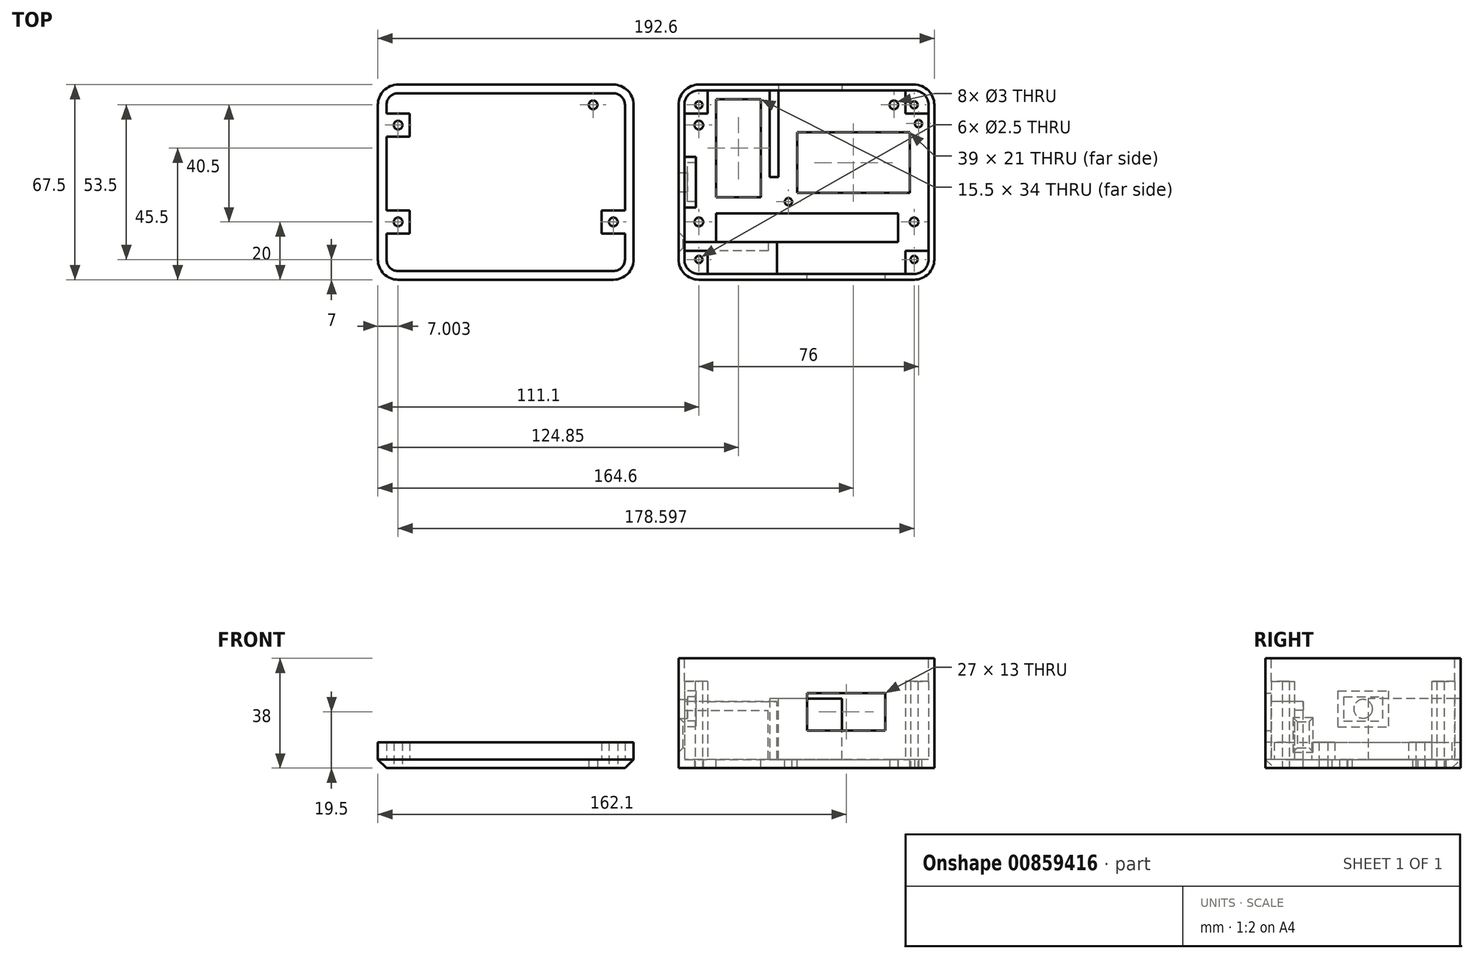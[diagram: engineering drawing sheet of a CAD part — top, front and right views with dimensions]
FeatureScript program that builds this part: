
annotation { "Feature Type Name" : "Feature", "Feature Type Description" : "" }
export const myFeature = defineFeature(function(context is Context, id is Id, definition is map)
    precondition{}
    {
        {
            var Q0;
            Q0=qCreatedBy(makeId("Top.planeOp"),FACE);
            var sketch = newSketch(context, id + "F0", { "sketchPlane" : qUnion([Q0])});
            skLineSegment(sketch, "E0.bottom", {"start": v(37.25, -30.75) * mm, "end": v(-37.25, -30.75) * mm});
            skLineSegment(sketch, "E0.top", {"start": v(37.25, 30.75) * mm, "end": v(-37.25, 30.75) * mm});
            skLineSegment(sketch, "E0.left", {"start": v(41.25, -26.75) * mm, "end": v(41.25, 26.75) * mm});
            skLineSegment(sketch, "E0.right", {"start": v(-41.25, -26.75) * mm, "end": v(-41.25, 26.75) * mm});
            skPoint(sketch, "E0.middle", {"position": v(0, 0) * mm});
            skPoint(sketch, "E1", {"position": v(-41.25, -26.75) * mm});
            skPoint(sketch, "E2", {"position": v(-41.25, 26.75) * mm});
            skPoint(sketch, "E3", {"position": v(37.25, -30.75) * mm});
            skPoint(sketch, "E4", {"position": v(-37.25, -30.75) * mm});
            skLineSegment(sketch, "E5", {"start": v(-41.25, 26.75) * mm, "end": v(41.25, 26.75) * mm, "construction": true});
            skLineSegment(sketch, "E6", {"start": v(-41.25, -26.75) * mm, "end": v(41.25, -26.75) * mm, "construction": true});
            skLineSegment(sketch, "E7", {"start": v(-37.25, -30.75) * mm, "end": v(-37.25, 30.75) * mm, "construction": true});
            skLineSegment(sketch, "E8", {"start": v(37.25, -30.75) * mm, "end": v(37.25, 30.75) * mm, "construction": true});
            skPoint(sketch, "E9", {"position": v(-37.25, 26.75) * mm});
            skPoint(sketch, "E10", {"position": v(37.25, 26.75) * mm});
            skPoint(sketch, "E11", {"position": v(37.25, -26.75) * mm});
            skPoint(sketch, "E12", {"position": v(-37.25, -26.75) * mm});
            skCircle(sketch, "E13", {"center": v(-37.25, 26.75) * mm, "radius": 1.25 * mm});
            skCircle(sketch, "E14", {"center": v(37.25, 26.75) * mm, "radius": 1.25 * mm});
            skCircle(sketch, "E15", {"center": v(-37.25, -26.75) * mm, "radius": 1.25 * mm});
            skCircle(sketch, "E16", {"center": v(37.25, -26.75) * mm, "radius": 1.25 * mm});
            skPoint(sketch, "E17.visualSharp", {"position": v(-41.25, 30.75) * mm});
            skArc(sketch, "E17.filletArc", {"start": v(-37.25, 30.75) * mm, "mid": v(-40.08, 29.58) * mm, "end": v(-41.25, 26.75) * mm});
            skPoint(sketch, "E18.visualSharp", {"position": v(41.25, 30.75) * mm});
            skArc(sketch, "E18.filletArc", {"start": v(41.25, 26.75) * mm, "mid": v(40.08, 29.58) * mm, "end": v(37.25, 30.75) * mm});
            skPoint(sketch, "E19.visualSharp", {"position": v(41.25, -30.75) * mm});
            skArc(sketch, "E19.filletArc", {"start": v(37.25, -30.75) * mm, "mid": v(40.08, -29.58) * mm, "end": v(41.25, -26.75) * mm});
            skPoint(sketch, "E20.visualSharp", {"position": v(-41.25, -30.75) * mm});
            skArc(sketch, "E20.filletArc", {"start": v(-41.25, -26.75) * mm, "mid": v(-40.08, -29.58) * mm, "end": v(-37.25, -30.75) * mm});
            skArc(sketch, "E21.0", {"start": v(44.25, 26.75) * mm, "mid": v(42.2, 31.7) * mm, "end": v(37.25, 33.75) * mm});
            skLineSegment(sketch, "E21.1", {"start": v(44.25, -26.75) * mm, "end": v(44.25, 26.75) * mm});
            skLineSegment(sketch, "E21.2", {"start": v(37.25, 33.75) * mm, "end": v(-37.25, 33.75) * mm});
            skArc(sketch, "E21.3", {"start": v(37.25, -33.75) * mm, "mid": v(42.2, -31.7) * mm, "end": v(44.25, -26.75) * mm});
            skArc(sketch, "E21.4", {"start": v(-37.25, 33.75) * mm, "mid": v(-42.2, 31.7) * mm, "end": v(-44.25, 26.75) * mm});
            skLineSegment(sketch, "E21.5", {"start": v(-44.25, -26.75) * mm, "end": v(-44.25, 26.75) * mm});
            skArc(sketch, "E21.6", {"start": v(-44.25, -26.75) * mm, "mid": v(-42.2, -31.7) * mm, "end": v(-37.25, -33.75) * mm});
            skLineSegment(sketch, "E21.7", {"start": v(37.25, -33.75) * mm, "end": v(-37.25, -33.75) * mm});
            skPoint(sketch, "E22", {"position": v(-41.25, 23.75) * mm});
            skPoint(sketch, "E23", {"position": v(-34.25, 30.75) * mm});
            skPoint(sketch, "E24", {"position": v(-41.25, -23.75) * mm});
            skPoint(sketch, "E25", {"position": v(-34.25, -30.75) * mm});
            skPoint(sketch, "E26", {"position": v(34.25, -30.75) * mm});
            skPoint(sketch, "E27", {"position": v(41.25, -23.75) * mm});
            skPoint(sketch, "E28", {"position": v(34.25, 30.75) * mm});
            skPoint(sketch, "E29", {"position": v(41.25, 23.75) * mm});
            skLineSegment(sketch, "E30", {"start": v(34.25, 30.75) * mm, "end": v(34.25, 23.75) * mm});
            skLineSegment(sketch, "E31", {"start": v(34.25, 23.75) * mm, "end": v(41.25, 23.75) * mm});
            skLineSegment(sketch, "E32", {"start": v(41.25, -23.75) * mm, "end": v(34.25, -23.75) * mm});
            skLineSegment(sketch, "E33", {"start": v(34.25, -23.75) * mm, "end": v(34.25, -30.75) * mm});
            skLineSegment(sketch, "E34", {"start": v(-34.25, -30.75) * mm, "end": v(-34.25, -23.75) * mm});
            skLineSegment(sketch, "E35", {"start": v(-34.25, -23.75) * mm, "end": v(-41.25, -23.75) * mm});
            skLineSegment(sketch, "E36", {"start": v(-41.25, 23.75) * mm, "end": v(-34.25, 23.75) * mm});
            skLineSegment(sketch, "E37", {"start": v(-34.25, 23.75) * mm, "end": v(-34.25, 30.75) * mm});
            skPoint(sketch, "E38", {"position": v(-37.25, -13.75) * mm});
            skPoint(sketch, "E39", {"position": v(37.25, -13.75) * mm});
            skPoint(sketch, "E40", {"position": v(-37.25, 19.75) * mm});
            skPoint(sketch, "E41", {"position": v(30.25, 26.75) * mm});
            skCircle(sketch, "E42", {"center": v(-37.25, 19.75) * mm, "radius": 1.5 * mm});
            skCircle(sketch, "E43", {"center": v(-37.25, -13.75) * mm, "radius": 1.5 * mm});
            skCircle(sketch, "E44", {"center": v(30.25, 26.75) * mm, "radius": 1.5 * mm});
            skCircle(sketch, "E45", {"center": v(37.25, -13.75) * mm, "radius": 1.5 * mm});
            skSolve(sketch);
        }
        {
            var Q0;
            {var subQ7=sQuery(id+"F0.wireOp",EDGE,"E30");Q0=makeQuery(id+"F0.imprint","IMPRINT",FACE,{"disambiguationData":[TD([[makeQuery(id+"F0.imprint","IMPRINT",EDGE,{"derivedFrom":subQ7}),-1.0]])]});}
            extrude(context, id + "F1", {"entities" : qUnion([Q0]), "depth" : 3 * mm, "offsetDistance" : 25 * mm});
        }
        {
            var Q0;
            Q0=makeQuery(id+"F0.imprint","IMPRINT",FACE,{"disambiguationData":[TD([[makeQuery(id+"F0.imprint","IMPRINT",EDGE,{"derivedFrom":sQuery(id+"F0.wireOp",EDGE,"E0.bottom")}),1.0]])]});
            extrude(context, id + "F2", {"entities" : qUnion([Q0]), "operationType" : NewBodyOperationType.ADD, "depth" : 38 * mm, "offsetDistance" : 25 * mm});
        }
        {
            var Q0;
            Q0=makeQuery(id+"F0.imprint","IMPRINT",FACE,{"disambiguationData":[TD([[makeQuery(id+"F0.imprint","IMPRINT",EDGE,{"derivedFrom":sQuery(id+"F0.wireOp",EDGE,"E13")}),-1.0]])]});
            var Q1;
            Q1=makeQuery(id+"F0.imprint","IMPRINT",FACE,{"disambiguationData":[TD([[makeQuery(id+"F0.imprint","IMPRINT",EDGE,{"derivedFrom":sQuery(id+"F0.wireOp",EDGE,"E15")}),-1.0]])]});
            var Q2;
            Q2=makeQuery(id+"F0.imprint","IMPRINT",FACE,{"disambiguationData":[TD([[makeQuery(id+"F0.imprint","IMPRINT",EDGE,{"derivedFrom":sQuery(id+"F0.wireOp",EDGE,"E14")}),-1.0]])]});
            var Q3;
            Q3=makeQuery(id+"F0.imprint","IMPRINT",FACE,{"disambiguationData":[TD([[makeQuery(id+"F0.imprint","IMPRINT",EDGE,{"derivedFrom":sQuery(id+"F0.wireOp",EDGE,"E16")}),-1.0]])]});
            extrude(context, id + "F3", {"entities" : qUnion([Q0, Q1, Q2, Q3]), "operationType" : NewBodyOperationType.ADD, "depth" : 30 * mm, "offsetDistance" : 25 * mm});
        }
        {
            var Q0;
            Q0=makeQuery(id+"F2.opExtrude","SWEPT_FACE",FACE,{"disambiguationData":[OSD([sQuery(id+"F0.wireOp",EDGE,"E0.bottom")])]});
            var sketch = newSketch(context, id + "F4", { "sketchPlane" : qUnion([Q0])});
            skLineSegment(sketch, "E46.bottom", {"start": v(34.25, 3) * mm, "end": v(13.25, 3) * mm});
            skLineSegment(sketch, "E46.top", {"start": v(34.25, 20) * mm, "end": v(13.25, 20) * mm});
            skLineSegment(sketch, "E46.left", {"start": v(34.25, 3) * mm, "end": v(34.25, 20) * mm});
            skLineSegment(sketch, "E46.right", {"start": v(13.25, 3) * mm, "end": v(13.25, 20) * mm});
            skLineSegment(sketch, "E47.0", {"start": v(10.25, 3) * mm, "end": v(10.25, 23) * mm});
            skLineSegment(sketch, "E47.1", {"start": v(34.25, 23) * mm, "end": v(10.25, 23) * mm});
            skLineSegment(sketch, "E48", {"start": v(34.25, 23) * mm, "end": v(34.25, 20) * mm});
            skLineSegment(sketch, "E49", {"start": v(13.25, 3) * mm, "end": v(10.25, 3) * mm});
            skPoint(sketch, "E50", {"position": v(-13.25, 3) * mm});
            skPoint(sketch, "E51", {"position": v(-13.25, 16) * mm});
            skLineSegment(sketch, "E52.top", {"start": v(-3.25, 26) * mm, "end": v(-27.25, 26) * mm});
            skLineSegment(sketch, "E52.right", {"start": v(-27.25, 16) * mm, "end": v(-27.25, 26) * mm});
            skLineSegment(sketch, "E53.0", {"start": v(-0.25, 13) * mm, "end": v(-0.25, 26) * mm});
            skLineSegment(sketch, "E53.1", {"start": v(-0.25, 13) * mm, "end": v(-27.25, 13) * mm});
            skLineSegment(sketch, "E54", {"start": v(-0.25, 26) * mm, "end": v(-3.25, 26) * mm});
            skLineSegment(sketch, "E55", {"start": v(-27.25, 13) * mm, "end": v(-27.25, 16) * mm});
            skSolve(sketch);
        }
        {
            var Q0;
            Q0=makeQuery(id+"F4.imprint","IMPRINT",FACE,{"disambiguationData":[TD([[makeQuery(id+"F4.imprint","IMPRINT",EDGE,{"derivedFrom":sQuery(id+"F4.wireOp",EDGE,"E46.top")}),-1.0]])]});
            var Q1;
            Q1=makeQuery(id+"F4.imprint","IMPRINT",FACE,{"disambiguationData":[TD([[makeQuery(id+"F4.imprint","IMPRINT",EDGE,{"derivedFrom":sQuery(id+"F4.wireOp",EDGE,"E46.bottom")}),1.0]])]});
            extrude(context, id + "F5", {"entities" : qUnion([Q0, Q1]), "operationType" : NewBodyOperationType.ADD, "depth" : 7 * mm, "offsetDistance" : 25 * mm});
        }
        {
            var Q0;
            Q0=makeQuery(id+"F5.boolean.opBoolean","MERGE",FACE,{"derivedFrom":[makeQuery(id+"F3.opExtrude","SWEPT_FACE",FACE,{"disambiguationData":[OSD([sQuery(id+"F0.wireOp",EDGE,"E35")])]}),makeQuery(id+"F5.opExtrude","CAP_FACE",FACE,{"disambiguationData":[OSD([sQuery(id+"F4.wireOp",EDGE,"E46.bottom"),sQuery(id+"F4.wireOp",EDGE,"E46.left"),sQuery(id+"F4.wireOp",EDGE,"E47.0"),sQuery(id+"F4.wireOp",EDGE,"E47.1"),sQuery(id+"F4.wireOp",EDGE,"E48"),sQuery(id+"F4.wireOp",EDGE,"E49")])],"isStart":false})]});
            var sketch = newSketch(context, id + "F6", { "sketchPlane" : qUnion([Q0])});
            skLineSegment(sketch, "E56", {"start": v(34.25, 23) * mm, "end": v(41.25, 23) * mm});
            skLineSegment(sketch, "E57.bottom", {"start": v(41.25, 3) * mm, "end": v(13.25, 3) * mm});
            skLineSegment(sketch, "E57.top", {"start": v(41.25, 20) * mm, "end": v(13.25, 20) * mm});
            skLineSegment(sketch, "E57.left", {"start": v(41.25, 3) * mm, "end": v(41.25, 20) * mm});
            skLineSegment(sketch, "E57.right", {"start": v(13.25, 3) * mm, "end": v(13.25, 20) * mm});
            skSolve(sketch);
        }
        {
            var Q0;
            {var subQ3=sQuery(id+"F6.wireOp",EDGE,"E56");Q0=makeQuery(id+"F6.imprint","IMPRINT",FACE,{"disambiguationData":[TD([[makeQuery(id+"F6.imprint","IMPRINT",EDGE,{"derivedFrom":subQ3}),-1.0]])]});}
            extrude(context, id + "F7", {"entities" : qUnion([Q0]), "operationType" : NewBodyOperationType.ADD, "depth" : 3 * mm, "offsetDistance" : 25 * mm});
        }
        {
            var Q0;
            Q0=makeQuery(id+"F2.opExtrude","SWEPT_FACE",FACE,{"disambiguationData":[OSD([sQuery(id+"F0.wireOp",EDGE,"E0.right")])]});
            var sketch = newSketch(context, id + "F8", { "sketchPlane" : qUnion([Q0])});
            skPoint(sketch, "E58", {"position": v(-23.75, 11.5) * mm});
            skPoint(sketch, "E59", {"position": v(-23.75, 16) * mm});
            skPoint(sketch, "E60", {"position": v(-23.75, 7) * mm});
            skLineSegment(sketch, "E61.bottom", {"start": v(-23.75, 16) * mm, "end": v(-18.75, 16) * mm});
            skLineSegment(sketch, "E61.top", {"start": v(-23.75, 7) * mm, "end": v(-18.75, 7) * mm});
            skLineSegment(sketch, "E61.right", {"start": v(-18.75, 16) * mm, "end": v(-18.75, 7) * mm});
            skPoint(sketch, "E62", {"position": v(-22.75, 16) * mm});
            skLineSegment(sketch, "E63", {"start": v(-22.75, 16) * mm, "end": v(-22.75, 7) * mm});
            skLineSegment(sketch, "E64", {"start": v(0, 3) * mm, "end": v(0, 38) * mm, "construction": true});
            skPoint(sketch, "E65", {"position": v(0, 20.5) * mm});
            skCircle(sketch, "E66", {"center": v(0, 20.5) * mm, "radius": 3.25 * mm});
            skLineSegment(sketch, "E67.bottom", {"start": v(-6.75, 24.75) * mm, "end": v(6.75, 24.75) * mm});
            skLineSegment(sketch, "E67.top", {"start": v(-6.75, 16.25) * mm, "end": v(6.75, 16.25) * mm});
            skLineSegment(sketch, "E67.left", {"start": v(-6.75, 24.75) * mm, "end": v(-6.75, 16.25) * mm});
            skLineSegment(sketch, "E67.right", {"start": v(6.75, 24.75) * mm, "end": v(6.75, 16.25) * mm});
            skLineSegment(sketch, "E68.0", {"start": v(-8.75, 26.75) * mm, "end": v(8.75, 26.75) * mm});
            skLineSegment(sketch, "E68.1", {"start": v(-8.75, 26.75) * mm, "end": v(-8.75, 14.25) * mm});
            skLineSegment(sketch, "E68.2", {"start": v(-8.75, 14.25) * mm, "end": v(8.75, 14.25) * mm});
            skLineSegment(sketch, "E68.3", {"start": v(8.75, 26.75) * mm, "end": v(8.75, 14.25) * mm});
            skSolve(sketch);
        }
        {
            var Q0;
            {var subQ0=sQuery(id+"F8.wireOp",EDGE,"E61.right");Q0=makeQuery(id+"F8.imprint","IMPRINT",FACE,{"disambiguationData":[TD([[makeQuery(id+"F8.imprint","IMPRINT",EDGE,{"derivedFrom":subQ0}),-1.0]])]});}
            extrude(context, id + "F9", {"entities" : qUnion([Q0]), "operationType" : NewBodyOperationType.REMOVE, "oppositeDirection" : true, "depth" : 25 * mm, "offsetDistance" : 25 * mm});
        }
        {
            var Q0;
            Q0=makeQuery(id+"F9.boolean.opBoolean","INTERSECT",EDGE,{"derivedFrom":[makeQuery(id+"F2.opExtrude","SWEPT_FACE",FACE,{"disambiguationData":[OSD([sQuery(id+"F0.wireOp",EDGE,"E21.5")])]}),makeQuery(id+"F9.opExtrude","SWEPT_FACE",FACE,{"disambiguationData":[OSD([sQuery(id+"F8.wireOp",EDGE,"E61.right")])]})]});
            var Q1;
            Q1=makeQuery(id+"F9.boolean.opBoolean","INTERSECT",EDGE,{"derivedFrom":[makeQuery(id+"F2.opExtrude","SWEPT_FACE",FACE,{"disambiguationData":[OSD([sQuery(id+"F0.wireOp",EDGE,"E21.5")])]}),makeQuery(id+"F9.opExtrude","SWEPT_FACE",FACE,{"disambiguationData":[OSD([sQuery(id+"F8.wireOp",EDGE,"E61.top")])]})]});
            var Q2;
            Q2=makeQuery(id+"F9.boolean.opBoolean","INTERSECT",EDGE,{"derivedFrom":[makeQuery(id+"F2.opExtrude","SWEPT_FACE",FACE,{"disambiguationData":[OSD([sQuery(id+"F0.wireOp",EDGE,"E21.5")])]}),makeQuery(id+"F9.opExtrude","SWEPT_FACE",FACE,{"disambiguationData":[OSD([sQuery(id+"F8.wireOp",EDGE,"E63")])]})]});
            var Q3;
            Q3=makeQuery(id+"F9.boolean.opBoolean","INTERSECT",EDGE,{"derivedFrom":[makeQuery(id+"F2.opExtrude","SWEPT_FACE",FACE,{"disambiguationData":[OSD([sQuery(id+"F0.wireOp",EDGE,"E21.5")])]}),makeQuery(id+"F9.opExtrude","SWEPT_FACE",FACE,{"disambiguationData":[OSD([sQuery(id+"F8.wireOp",EDGE,"E61.bottom")])]})]});
            chamfer(context, id + "F10", {"entities" : qUnion([Q0, Q1, Q2, Q3]), "width" : 1.5 * mm, "tangentPropagation" : true});
        }
        {
            var Q0;
            Q0=makeQuery(id+"F1.opExtrude","CAP_FACE",FACE,{"disambiguationData":[OSD([sQuery(id+"F0.wireOp",EDGE,"E0.bottom"),sQuery(id+"F0.wireOp",EDGE,"E0.top"),sQuery(id+"F0.wireOp",EDGE,"E0.left"),sQuery(id+"F0.wireOp",EDGE,"E0.right"),sQuery(id+"F0.wireOp",EDGE,"E30"),sQuery(id+"F0.wireOp",EDGE,"E31"),sQuery(id+"F0.wireOp",EDGE,"E32"),sQuery(id+"F0.wireOp",EDGE,"E33"),sQuery(id+"F0.wireOp",EDGE,"E34"),sQuery(id+"F0.wireOp",EDGE,"E35"),sQuery(id+"F0.wireOp",EDGE,"E36"),sQuery(id+"F0.wireOp",EDGE,"E37")])],"isStart":false});
            var sketch = newSketch(context, id + "F11", { "sketchPlane" : qUnion([Q0])});
            skPoint(sketch, "E69", {"position": v(12.25, 21.25) * mm});
            skPoint(sketch, "E70", {"position": v(-8.75, 21.25) * mm});
            skPoint(sketch, "E71", {"position": v(-8.75, 30.75) * mm});
            skPoint(sketch, "E72", {"position": v(12.25, 30.75) * mm});
            skLineSegment(sketch, "E73", {"start": v(-34.25, 26.75) * mm, "end": v(-34.25, 23.75) * mm});
            skLineSegment(sketch, "E74", {"start": v(-6.25, -11.75) * mm, "end": v(41.25, -11.75) * mm});
            skCircle(sketch, "E75", {"center": v(38.75, 20.25) * mm, "radius": 1.25 * mm});
            skLineSegment(sketch, "E76", {"start": v(38.75, 20.25) * mm, "end": v(41.25, 20.25) * mm});
            skLineSegment(sketch, "E77", {"start": v(-6.25, -11.75) * mm, "end": v(-6.25, -6.75) * mm});
            skCircle(sketch, "E78", {"center": v(-6.25, -6.75) * mm, "radius": 1.25 * mm});
            skLineSegment(sketch, "E79.bottom", {"start": v(-6.25, -6.75) * mm, "end": v(38.75, -6.75) * mm});
            skLineSegment(sketch, "E79.top", {"start": v(-6.25, 20.25) * mm, "end": v(38.75, 20.25) * mm});
            skLineSegment(sketch, "E79.left", {"start": v(-6.25, -6.75) * mm, "end": v(-6.25, 20.25) * mm});
            skLineSegment(sketch, "E79.right", {"start": v(38.75, -6.75) * mm, "end": v(38.75, 20.25) * mm});
            skLineSegment(sketch, "E80.0", {"start": v(-3.25, -3.75) * mm, "end": v(35.75, -3.75) * mm});
            skLineSegment(sketch, "E80.1", {"start": v(-3.25, -3.75) * mm, "end": v(-3.25, 17.25) * mm});
            skLineSegment(sketch, "E80.2", {"start": v(-3.25, 17.25) * mm, "end": v(35.75, 17.25) * mm});
            skLineSegment(sketch, "E80.3", {"start": v(35.75, -3.75) * mm, "end": v(35.75, 17.25) * mm});
            skSolve(sketch);
        }
        {
            var Q0;
            Q0=makeQuery(id+"F2.opExtrude","SWEPT_FACE",FACE,{"disambiguationData":[OSD([sQuery(id+"F0.wireOp",EDGE,"E0.top")])]});
            var sketch = newSketch(context, id + "F12", { "sketchPlane" : qUnion([Q0])});
            skPoint(sketch, "E81", {"position": v(12.25, 3) * mm});
            skLineSegment(sketch, "E82.bottom", {"start": v(12.25, 3) * mm, "end": v(-8.75, 3) * mm});
            skLineSegment(sketch, "E82.top", {"start": v(12.25, 24) * mm, "end": v(-8.75, 24) * mm});
            skLineSegment(sketch, "E82.left", {"start": v(12.25, 3) * mm, "end": v(12.25, 24) * mm});
            skLineSegment(sketch, "E82.right", {"start": v(-8.75, 3) * mm, "end": v(-8.75, 24) * mm});
            skSolve(sketch);
        }
        {
            var Q0;
            Q0=makeQuery(id+"F12.imprint","IMPRINT",FACE,{"disambiguationData":[TD([[makeQuery(id+"F12.imprint","IMPRINT",EDGE,{"derivedFrom":sQuery(id+"F12.wireOp",EDGE,"E82.bottom")}),-1.0]])]});
            extrude(context, id + "F13", {"entities" : qUnion([Q0]), "operationType" : NewBodyOperationType.REMOVE, "oppositeDirection" : true, "depth" : 25 * mm, "offsetDistance" : 25 * mm});
        }
        {
            var Q0;
            Q0=makeQuery(id+"F4.imprint","IMPRINT",FACE,{"disambiguationData":[TD([[makeQuery(id+"F4.imprint","IMPRINT",EDGE,{"derivedFrom":sQuery(id+"F4.wireOp",EDGE,"E52.top")}),1.0]])]});
            extrude(context, id + "F14", {"entities" : qUnion([Q0]), "operationType" : NewBodyOperationType.REMOVE, "oppositeDirection" : true, "depth" : 25 * mm, "offsetDistance" : 25 * mm});
        }
        {
            var Q0;
            Q0=qCreatedBy(makeId("Top.planeOp"),FACE);
            var sketch = newSketch(context, id + "F15", { "sketchPlane" : qUnion([Q0])});
            skLineSegment(sketch, "E83.bottom", {"start": v(-66.85, -30.75) * mm, "end": v(-141.35, -30.75) * mm});
            skLineSegment(sketch, "E83.top", {"start": v(-66.85, 30.75) * mm, "end": v(-141.35, 30.75) * mm});
            skLineSegment(sketch, "E83.left", {"start": v(-62.85, -26.75) * mm, "end": v(-62.85, 26.75) * mm});
            skLineSegment(sketch, "E83.right", {"start": v(-145.35, -26.75) * mm, "end": v(-145.35, 26.75) * mm});
            skPoint(sketch, "E83.middle", {"position": v(-104.1, 0) * mm});
            skPoint(sketch, "E84", {"position": v(-145.35, -26.75) * mm});
            skPoint(sketch, "E85", {"position": v(-145.35, 26.75) * mm});
            skPoint(sketch, "E86", {"position": v(-66.85, -30.75) * mm});
            skPoint(sketch, "E87", {"position": v(-141.35, -30.75) * mm});
            skLineSegment(sketch, "E88", {"start": v(-145.35, 26.75) * mm, "end": v(-62.85, 26.75) * mm, "construction": true});
            skLineSegment(sketch, "E89", {"start": v(-145.35, -26.75) * mm, "end": v(-62.85, -26.75) * mm, "construction": true});
            skLineSegment(sketch, "E90", {"start": v(-141.35, -30.75) * mm, "end": v(-141.35, 30.75) * mm, "construction": true});
            skLineSegment(sketch, "E91", {"start": v(-66.85, -30.75) * mm, "end": v(-66.85, 30.75) * mm, "construction": true});
            skPoint(sketch, "E92", {"position": v(-141.35, 26.75) * mm});
            skPoint(sketch, "E93", {"position": v(-66.85, 26.75) * mm});
            skPoint(sketch, "E94", {"position": v(-66.85, -26.75) * mm});
            skPoint(sketch, "E95", {"position": v(-141.35, -26.75) * mm});
            skCircle(sketch, "E96", {"center": v(-141.35, 26.75) * mm, "radius": 1.25 * mm});
            skCircle(sketch, "E97", {"center": v(-66.85, 26.75) * mm, "radius": 1.25 * mm});
            skCircle(sketch, "E98", {"center": v(-141.35, -26.75) * mm, "radius": 1.25 * mm});
            skCircle(sketch, "E99", {"center": v(-66.85, -26.75) * mm, "radius": 1.25 * mm});
            skPoint(sketch, "E100.visualSharp", {"position": v(-145.35, 30.75) * mm});
            skArc(sketch, "E100.filletArc", {"start": v(-141.35, 30.75) * mm, "mid": v(-144.18, 29.58) * mm, "end": v(-145.35, 26.75) * mm});
            skPoint(sketch, "E101.visualSharp", {"position": v(-62.85, 30.75) * mm});
            skArc(sketch, "E101.filletArc", {"start": v(-62.85, 26.75) * mm, "mid": v(-64.02, 29.58) * mm, "end": v(-66.85, 30.75) * mm});
            skPoint(sketch, "E102.visualSharp", {"position": v(-62.85, -30.75) * mm});
            skArc(sketch, "E102.filletArc", {"start": v(-66.85, -30.75) * mm, "mid": v(-64.02, -29.58) * mm, "end": v(-62.85, -26.75) * mm});
            skPoint(sketch, "E103.visualSharp", {"position": v(-145.35, -30.75) * mm});
            skArc(sketch, "E103.filletArc", {"start": v(-145.35, -26.75) * mm, "mid": v(-144.18, -29.58) * mm, "end": v(-141.35, -30.75) * mm});
            skArc(sketch, "E104.0", {"start": v(-59.85, 26.75) * mm, "mid": v(-61.9, 31.7) * mm, "end": v(-66.85, 33.75) * mm});
            skLineSegment(sketch, "E104.1", {"start": v(-59.85, -26.75) * mm, "end": v(-59.85, 26.75) * mm});
            skLineSegment(sketch, "E104.2", {"start": v(-66.85, 33.75) * mm, "end": v(-141.35, 33.75) * mm});
            skArc(sketch, "E104.3", {"start": v(-66.85, -33.75) * mm, "mid": v(-61.9, -31.7) * mm, "end": v(-59.85, -26.75) * mm});
            skArc(sketch, "E104.4", {"start": v(-141.35, 33.75) * mm, "mid": v(-146.3, 31.7) * mm, "end": v(-148.35, 26.75) * mm});
            skLineSegment(sketch, "E104.5", {"start": v(-148.35, -26.75) * mm, "end": v(-148.35, 26.75) * mm});
            skArc(sketch, "E104.6", {"start": v(-148.35, -26.75) * mm, "mid": v(-146.3, -31.7) * mm, "end": v(-141.35, -33.75) * mm});
            skLineSegment(sketch, "E104.7", {"start": v(-66.85, -33.75) * mm, "end": v(-141.35, -33.75) * mm});
            skPoint(sketch, "E105", {"position": v(-145.35, 23.75) * mm});
            skPoint(sketch, "E106", {"position": v(-138.35, 30.75) * mm});
            skPoint(sketch, "E107", {"position": v(-145.35, -23.75) * mm});
            skPoint(sketch, "E108", {"position": v(-138.35, -30.75) * mm});
            skPoint(sketch, "E109", {"position": v(-69.85, -30.75) * mm});
            skPoint(sketch, "E110", {"position": v(-62.85, -23.75) * mm});
            skPoint(sketch, "E111", {"position": v(-69.85, 30.75) * mm});
            skPoint(sketch, "E112", {"position": v(-62.85, 23.75) * mm});
            skLineSegment(sketch, "E113", {"start": v(-69.85, 30.75) * mm, "end": v(-69.85, 23.75) * mm});
            skLineSegment(sketch, "E114", {"start": v(-69.85, 23.75) * mm, "end": v(-62.85, 23.75) * mm});
            skLineSegment(sketch, "E115", {"start": v(-62.85, -23.75) * mm, "end": v(-69.85, -23.75) * mm});
            skLineSegment(sketch, "E116", {"start": v(-69.85, -23.75) * mm, "end": v(-69.85, -30.75) * mm});
            skLineSegment(sketch, "E117", {"start": v(-138.35, -30.75) * mm, "end": v(-138.35, -23.75) * mm});
            skLineSegment(sketch, "E118", {"start": v(-138.35, -23.75) * mm, "end": v(-145.35, -23.75) * mm});
            skLineSegment(sketch, "E119", {"start": v(-145.35, 23.75) * mm, "end": v(-138.35, 23.75) * mm});
            skLineSegment(sketch, "E120", {"start": v(-138.35, 23.75) * mm, "end": v(-138.35, 30.75) * mm});
            skPoint(sketch, "E121", {"position": v(-141.35, 19.75) * mm});
            skPoint(sketch, "E122", {"position": v(-141.35, -13.75) * mm});
            skPoint(sketch, "E123", {"position": v(-66.85, -13.75) * mm});
            skCircle(sketch, "E124", {"center": v(-141.35, 19.75) * mm, "radius": 1.5 * mm});
            skCircle(sketch, "E125", {"center": v(-141.35, -13.75) * mm, "radius": 1.5 * mm});
            skCircle(sketch, "E126", {"center": v(-66.85, -13.75) * mm, "radius": 1.5 * mm});
            skLineSegment(sketch, "E127.bottom", {"start": v(-145.35, 23.75) * mm, "end": v(-137.35, 23.75) * mm});
            skLineSegment(sketch, "E127.top", {"start": v(-145.35, 15.75) * mm, "end": v(-137.35, 15.75) * mm});
            skLineSegment(sketch, "E127.left", {"start": v(-145.35, 23.75) * mm, "end": v(-145.35, 15.75) * mm});
            skLineSegment(sketch, "E127.right", {"start": v(-137.35, 23.75) * mm, "end": v(-137.35, 15.75) * mm});
            skLineSegment(sketch, "E128.bottom", {"start": v(-145.35, -23.75) * mm, "end": v(-138.35, -23.75) * mm});
            skLineSegment(sketch, "E129.bottom", {"start": v(-62.85, 23.75) * mm, "end": v(-70.85, 23.75) * mm});
            skLineSegment(sketch, "E129.left", {"start": v(-62.85, 23.75) * mm, "end": v(-62.85, 15.75) * mm});
            skLineSegment(sketch, "E130.bottom", {"start": v(-62.85, -23.75) * mm, "end": v(-70.85, -23.75) * mm});
            skLineSegment(sketch, "E130.left", {"start": v(-62.85, -23.75) * mm, "end": v(-62.85, -3.75) * mm});
            skLineSegment(sketch, "E131.bottom", {"start": v(-145.35, -17.75) * mm, "end": v(-137.35, -17.75) * mm});
            skLineSegment(sketch, "E131.top", {"start": v(-145.35, -9.75) * mm, "end": v(-137.35, -9.75) * mm});
            skLineSegment(sketch, "E131.left", {"start": v(-145.35, -17.75) * mm, "end": v(-145.35, -9.75) * mm});
            skLineSegment(sketch, "E131.right", {"start": v(-137.35, -17.75) * mm, "end": v(-137.35, -9.75) * mm});
            skPoint(sketch, "E132", {"position": v(-73.85, 26.75) * mm});
            skLineSegment(sketch, "E133.bottom", {"start": v(-69.85, 30.75) * mm, "end": v(-77.85, 30.75) * mm});
            skLineSegment(sketch, "E133.top", {"start": v(-69.85, 22.75) * mm, "end": v(-77.85, 22.75) * mm});
            skLineSegment(sketch, "E133.left", {"start": v(-69.85, 30.75) * mm, "end": v(-69.85, 22.75) * mm});
            skLineSegment(sketch, "E133.right", {"start": v(-77.85, 30.75) * mm, "end": v(-77.85, 22.75) * mm});
            skLineSegment(sketch, "E134.bottom", {"start": v(-62.85, -9.75) * mm, "end": v(-70.85, -9.75) * mm});
            skLineSegment(sketch, "E134.top", {"start": v(-62.85, -17.75) * mm, "end": v(-70.85, -17.75) * mm});
            skLineSegment(sketch, "E134.left", {"start": v(-62.85, -9.75) * mm, "end": v(-62.85, -17.75) * mm});
            skLineSegment(sketch, "E134.right", {"start": v(-70.85, -9.75) * mm, "end": v(-70.85, -17.75) * mm});
            skCircle(sketch, "E135", {"center": v(-73.85, 26.75) * mm, "radius": 1.5 * mm});
            skSolve(sketch);
        }
        {
            var Q0;
            {var subQ7=sQuery(id+"F15.wireOp",EDGE,"E113");Q0=makeQuery(id+"F15.imprint","IMPRINT",FACE,{"disambiguationData":[TD([[makeQuery(id+"F15.imprint","IMPRINT",EDGE,{"derivedFrom":subQ7}),-1.0]])]});}
            var Q1;
            Q1=makeQuery(id+"F15.imprint","IMPRINT",FACE,{"disambiguationData":[TD([[makeQuery(id+"F15.imprint","IMPRINT",EDGE,{"derivedFrom":sQuery(id+"F15.wireOp",EDGE,"E97")}),-1.0]])]});
            var Q2;
            Q2=makeQuery(id+"F15.imprint","IMPRINT",FACE,{"disambiguationData":[TD([[makeQuery(id+"F15.imprint","IMPRINT",EDGE,{"derivedFrom":sQuery(id+"F15.wireOp",EDGE,"E97")}),1.0]])]});
            var Q3;
            Q3=makeQuery(id+"F15.imprint","IMPRINT",FACE,{"disambiguationData":[TD([[makeQuery(id+"F15.imprint","IMPRINT",EDGE,{"derivedFrom":sQuery(id+"F15.wireOp",EDGE,"E99")}),1.0]])]});
            var Q4;
            Q4=makeQuery(id+"F15.imprint","IMPRINT",FACE,{"disambiguationData":[TD([[makeQuery(id+"F15.imprint","IMPRINT",EDGE,{"derivedFrom":sQuery(id+"F15.wireOp",EDGE,"E99")}),-1.0]])]});
            var Q5;
            Q5=makeQuery(id+"F15.imprint","IMPRINT",FACE,{"disambiguationData":[TD([[makeQuery(id+"F15.imprint","IMPRINT",EDGE,{"derivedFrom":sQuery(id+"F15.wireOp",EDGE,"E98")}),1.0]])]});
            var Q6;
            Q6=makeQuery(id+"F15.imprint","IMPRINT",FACE,{"disambiguationData":[TD([[makeQuery(id+"F15.imprint","IMPRINT",EDGE,{"derivedFrom":sQuery(id+"F15.wireOp",EDGE,"E98")}),-1.0]])]});
            var Q7;
            Q7=makeQuery(id+"F15.imprint","IMPRINT",FACE,{"disambiguationData":[TD([[makeQuery(id+"F15.imprint","IMPRINT",EDGE,{"derivedFrom":sQuery(id+"F15.wireOp",EDGE,"E96")}),-1.0]])]});
            var Q8;
            Q8=makeQuery(id+"F15.imprint","IMPRINT",FACE,{"disambiguationData":[TD([[makeQuery(id+"F15.imprint","IMPRINT",EDGE,{"derivedFrom":sQuery(id+"F15.wireOp",EDGE,"E96")}),1.0]])]});
            var Q9;
            {var subQ13=sQuery(id+"F15.wireOp",EDGE,"E116");Q9=makeQuery(id+"F15.imprint","IMPRINT",FACE,{"disambiguationData":[TD([[makeQuery(id+"F15.imprint","IMPRINT",EDGE,{"derivedFrom":subQ13}),-1.0]])]});}
            extrude(context, id + "F16", {"entities" : qUnion([Q0, Q1, Q2, Q3, Q4, Q5, Q6, Q7, Q8, Q9]), "depth" : 3 * mm, "offsetDistance" : 25 * mm});
        }
        {
            var Q0;
            {var subQ3=sQuery(id+"F15.wireOp",EDGE,"E100.filletArc");Q0=makeQuery(id+"F15.imprint","IMPRINT",FACE,{"disambiguationData":[TD([[makeQuery(id+"F15.imprint","IMPRINT",EDGE,{"derivedFrom":subQ3}),-1.0]])]});}
            var Q1;
            Q1=makeQuery(id+"F15.imprint","IMPRINT",FACE,{"disambiguationData":[TD([[makeQuery(id+"F15.imprint","IMPRINT",EDGE,{"derivedFrom":sQuery(id+"F15.wireOp",EDGE,"E125")}),-1.0]])]});
            var Q2;
            Q2=makeQuery(id+"F15.imprint","IMPRINT",FACE,{"disambiguationData":[TD([[makeQuery(id+"F15.imprint","IMPRINT",EDGE,{"derivedFrom":sQuery(id+"F15.wireOp",EDGE,"E124")}),-1.0]])]});
            var Q3;
            Q3=makeQuery(id+"F15.imprint","IMPRINT",FACE,{"disambiguationData":[TD([[makeQuery(id+"F15.imprint","IMPRINT",EDGE,{"derivedFrom":sQuery(id+"F15.wireOp",EDGE,"FU00ZgID-8B0F-kORG-vy9U-vkuXLLqvUof6")}),-1.0]])]});
            var Q4;
            Q4=makeQuery(id+"F15.imprint","IMPRINT",FACE,{"disambiguationData":[TD([[makeQuery(id+"F15.imprint","IMPRINT",EDGE,{"derivedFrom":sQuery(id+"F15.wireOp",EDGE,"E126")}),-1.0]])]});
            var Q5;
            {var subQ3=sQuery(id+"F15.wireOp",EDGE,"E133.bottom");Q5=makeQuery(id+"F15.imprint","IMPRINT",FACE,{"disambiguationData":[TD([[makeQuery(id+"F15.imprint","IMPRINT",EDGE,{"derivedFrom":subQ3}),1.0]])]});}
            extrude(context, id + "F17", {"entities" : qUnion([Q0, Q1, Q2, Q3, Q4, Q5]), "operationType" : NewBodyOperationType.ADD, "depth" : 9 * mm, "offsetDistance" : 25 * mm});
        }
        {
            var Q0;
            Q0=makeQuery(id+"F17.opExtrude","CAP_EDGE",EDGE,{"disambiguationData":[OSD([sQuery(id+"F15.wireOp",EDGE,"E104.7")])],"isStart":true});
            var Q1;
            Q1=makeQuery(id+"F17.opExtrude","CAP_EDGE",EDGE,{"disambiguationData":[OSD([sQuery(id+"F15.wireOp",EDGE,"E104.3")])],"isStart":true});
            var Q2;
            Q2=makeQuery(id+"F17.opExtrude","CAP_EDGE",EDGE,{"disambiguationData":[OSD([sQuery(id+"F15.wireOp",EDGE,"E104.1")])],"isStart":true});
            var Q3;
            Q3=makeQuery(id+"F17.opExtrude","CAP_EDGE",EDGE,{"disambiguationData":[OSD([sQuery(id+"F15.wireOp",EDGE,"E104.0")])],"isStart":true});
            var Q4;
            Q4=makeQuery(id+"F17.opExtrude","CAP_EDGE",EDGE,{"disambiguationData":[OSD([sQuery(id+"F15.wireOp",EDGE,"E104.2")])],"isStart":true});
            var Q5;
            Q5=makeQuery(id+"F17.opExtrude","CAP_EDGE",EDGE,{"disambiguationData":[OSD([sQuery(id+"F15.wireOp",EDGE,"E104.4")])],"isStart":true});
            var Q6;
            Q6=makeQuery(id+"F17.opExtrude","CAP_EDGE",EDGE,{"disambiguationData":[OSD([sQuery(id+"F15.wireOp",EDGE,"E104.5")])],"isStart":true});
            var Q7;
            Q7=makeQuery(id+"F17.opExtrude","CAP_EDGE",EDGE,{"disambiguationData":[OSD([sQuery(id+"F15.wireOp",EDGE,"E104.6")])],"isStart":true});
            chamfer(context, id + "F18", {"entities" : qUnion([Q0, Q1, Q2, Q3, Q4, Q5, Q6, Q7]), "width" : 3 * mm, "tangentPropagation" : true});
        }
        {
            var Q0;
            Q0=makeQuery(id+"F11.imprint","IMPRINT",FACE,{"disambiguationData":[TD([[makeQuery(id+"F11.imprint","IMPRINT",EDGE,{"derivedFrom":sQuery(id+"F11.wireOp",EDGE,"E75")}),1.0]])]});
            var Q1;
            Q1=makeQuery(id+"F11.imprint","IMPRINT",FACE,{"disambiguationData":[TD([[makeQuery(id+"F11.imprint","IMPRINT",EDGE,{"derivedFrom":sQuery(id+"F11.wireOp",EDGE,"i0QRaYDh-TXxo-nYKi-BQN7-LDAzg9FkCDSr")}),1.0]])]});
            extrude(context, id + "F19", {"entities" : qUnion([Q0, Q1]), "operationType" : NewBodyOperationType.REMOVE, "oppositeDirection" : true, "depth" : 25 * mm, "offsetDistance" : 25 * mm});
        }
        {
            var Q0;
            Q0=makeQuery(id+"F8.imprint","IMPRINT",FACE,{"disambiguationData":[TD([[makeQuery(id+"F8.imprint","IMPRINT",EDGE,{"derivedFrom":sQuery(id+"F8.wireOp",EDGE,"E67.bottom")}),1.0]])]});
            extrude(context, id + "F20", {"entities" : qUnion([Q0]), "operationType" : NewBodyOperationType.ADD, "depth" : 4 * mm, "offsetDistance" : 25 * mm});
        }
        {
            var Q0;
            Q0=makeQuery(id+"F8.imprint","IMPRINT",FACE,{"disambiguationData":[TD([[makeQuery(id+"F8.imprint","IMPRINT",EDGE,{"derivedFrom":sQuery(id+"F8.wireOp",EDGE,"E66")}),1.0]])]});
            extrude(context, id + "F21", {"entities" : qUnion([Q0]), "operationType" : NewBodyOperationType.REMOVE, "oppositeDirection" : true, "depth" : 25 * mm, "offsetDistance" : 25 * mm});
        }
        {
            var Q0;
            Q0=makeQuery(id+"F2.opExtrude","CAP_FACE",FACE,{"disambiguationData":[OSD([sQuery(id+"F0.wireOp",EDGE,"E0.bottom"),sQuery(id+"F0.wireOp",EDGE,"E0.top"),sQuery(id+"F0.wireOp",EDGE,"E0.left"),sQuery(id+"F0.wireOp",EDGE,"E0.right"),sQuery(id+"F0.wireOp",EDGE,"E17.filletArc"),sQuery(id+"F0.wireOp",EDGE,"E18.filletArc"),sQuery(id+"F0.wireOp",EDGE,"E19.filletArc"),sQuery(id+"F0.wireOp",EDGE,"E20.filletArc"),sQuery(id+"F0.wireOp",EDGE,"E21.0"),sQuery(id+"F0.wireOp",EDGE,"E21.1"),sQuery(id+"F0.wireOp",EDGE,"E21.2"),sQuery(id+"F0.wireOp",EDGE,"E21.3"),sQuery(id+"F0.wireOp",EDGE,"E21.4"),sQuery(id+"F0.wireOp",EDGE,"E21.5"),sQuery(id+"F0.wireOp",EDGE,"E21.6"),sQuery(id+"F0.wireOp",EDGE,"E21.7")])],"isStart":false});
            var sketch = newSketch(context, id + "F22", { "sketchPlane" : qUnion([Q0])});
            skArc(sketch, "E136.0", {"start": v(-42.25, -26.75) * mm, "mid": v(-40.79, -30.29) * mm, "end": v(-37.25, -31.75) * mm});
            skLineSegment(sketch, "E136.1", {"start": v(37.25, -31.75) * mm, "end": v(-37.25, -31.75) * mm});
            skLineSegment(sketch, "E136.2", {"start": v(-42.25, -26.75) * mm, "end": v(-42.25, 26.75) * mm});
            skArc(sketch, "E136.3", {"start": v(37.25, -31.75) * mm, "mid": v(40.79, -30.29) * mm, "end": v(42.25, -26.75) * mm});
            skArc(sketch, "E136.4", {"start": v(-37.25, 31.75) * mm, "mid": v(-40.79, 30.29) * mm, "end": v(-42.25, 26.75) * mm});
            skLineSegment(sketch, "E136.5", {"start": v(37.25, 31.75) * mm, "end": v(-37.25, 31.75) * mm});
            skArc(sketch, "E136.6", {"start": v(42.25, 26.75) * mm, "mid": v(40.79, 30.29) * mm, "end": v(37.25, 31.75) * mm});
            skLineSegment(sketch, "E136.7", {"start": v(42.25, -26.75) * mm, "end": v(42.25, 26.75) * mm});
            skSolve(sketch);
        }
        {
            var Q0;
            Q0=makeQuery(id+"F22.imprint","IMPRINT",FACE,{"disambiguationData":[TD([[makeQuery(id+"F22.imprint","IMPRINT",EDGE,{"derivedFrom":sQuery(id+"F22.wireOp",EDGE,"E136.0")}),1.0]])]});
            extrude(context, id + "F23", {"entities" : qUnion([Q0]), "operationType" : NewBodyOperationType.REMOVE, "oppositeDirection" : true, "depth" : 8 * mm, "offsetDistance" : 25 * mm});
        }
        {
            var Q0;
            {var subQ6=sQuery(id+"F0.wireOp",EDGE,"E17.filletArc");var subQ7=sQuery(id+"F0.wireOp",EDGE,"E0.right");Q0=makeQuery(id+"F20.boolean.opBoolean","SPLIT",FACE,{"disambiguationData":[TD([makeQuery(id+"F2.opExtrude","SWEPT_FACE",FACE,{"disambiguationData":[OSD([subQ6])]})])],"derivedFrom":makeQuery(id+"F2.opExtrude","SWEPT_FACE",FACE,{"disambiguationData":[OSD([subQ7])]})});}
            extrude(context, id + "F24", {"entities" : qUnion([Q0]), "operationType" : NewBodyOperationType.REMOVE, "oppositeDirection" : true, "depth" : 1 * mm, "offsetDistance" : 25 * mm});
        }
        {
            var Q0;
            Q0=makeQuery(id+"F2.opExtrude","SWEPT_FACE",FACE,{"disambiguationData":[OSD([sQuery(id+"F0.wireOp",EDGE,"E0.top")])]});
            extrude(context, id + "F25", {"entities" : qUnion([Q0]), "operationType" : NewBodyOperationType.REMOVE, "oppositeDirection" : true, "depth" : 1 * mm, "offsetDistance" : 25 * mm});
        }
        {
            var Q0;
            Q0=makeQuery(id+"F2.opExtrude","SWEPT_FACE",FACE,{"disambiguationData":[OSD([sQuery(id+"F0.wireOp",EDGE,"E0.left")])]});
            extrude(context, id + "F26", {"entities" : qUnion([Q0]), "operationType" : NewBodyOperationType.REMOVE, "oppositeDirection" : true, "depth" : 1 * mm, "offsetDistance" : 25 * mm});
        }
        {
            var Q0;
            Q0=makeQuery(id+"F2.opExtrude","SWEPT_FACE",FACE,{"disambiguationData":[OSD([sQuery(id+"F0.wireOp",EDGE,"E0.bottom")])]});
            extrude(context, id + "F27", {"entities" : qUnion([Q0]), "operationType" : NewBodyOperationType.REMOVE, "oppositeDirection" : true, "depth" : 1 * mm, "offsetDistance" : 25 * mm});
        }
        {
            var Q0;
            Q0=makeQuery(id+"F20.opExtrude","CAP_FACE",FACE,{"disambiguationData":[OSD([sQuery(id+"F8.wireOp",EDGE,"E67.bottom"),sQuery(id+"F8.wireOp",EDGE,"E67.top"),sQuery(id+"F8.wireOp",EDGE,"E67.left"),sQuery(id+"F8.wireOp",EDGE,"E67.right"),sQuery(id+"F8.wireOp",EDGE,"E68.0"),sQuery(id+"F8.wireOp",EDGE,"E68.1"),sQuery(id+"F8.wireOp",EDGE,"E68.2"),sQuery(id+"F8.wireOp",EDGE,"E68.3")])],"isStart":false});
            extrude(context, id + "F28", {"entities" : qUnion([Q0]), "operationType" : NewBodyOperationType.REMOVE, "oppositeDirection" : true, "depth" : 1 * mm, "offsetDistance" : 25 * mm});
        }
        {
            var Q0;
            {var subQ0=sQuery(id+"F0.wireOp",EDGE,"E0.bottom");var subQ1=sQuery(id+"F0.wireOp",EDGE,"E0.left");var subQ2=makeQuery(id+"F13.opExtrude","SWEPT_FACE",FACE,{"disambiguationData":[OSD([sQuery(id+"F12.wireOp",EDGE,"E82.bottom")])]});var subQ3=sQuery(id+"F0.wireOp",EDGE,"E37");var subQ4=sQuery(id+"F0.wireOp",EDGE,"E0.top");var subQ6=sQuery(id+"F0.wireOp",EDGE,"E30");var subQ7=sQuery(id+"F0.wireOp",EDGE,"E0.right");var subQ8=makeQuery(id+"F1.opExtrude","CAP_FACE",FACE,{"disambiguationData":[OSD([subQ0,subQ4,subQ1,subQ7,subQ6,sQuery(id+"F0.wireOp",EDGE,"E31"),sQuery(id+"F0.wireOp",EDGE,"E32"),sQuery(id+"F0.wireOp",EDGE,"E33"),sQuery(id+"F0.wireOp",EDGE,"E34"),sQuery(id+"F0.wireOp",EDGE,"E35"),sQuery(id+"F0.wireOp",EDGE,"E36"),subQ3,sQuery(id+"F0.wireOp",EDGE,"E42"),sQuery(id+"F0.wireOp",EDGE,"E43"),sQuery(id+"F0.wireOp",EDGE,"E44"),sQuery(id+"F0.wireOp",EDGE,"E45")])],"isStart":false});var subQ9=makeQuery(id+"F1.opExtrude","CAP_EDGE",EDGE,{"disambiguationData":[OSD([subQ4])],"isStart":false});Q0=makeQuery(id+"F27.boolean.opBoolean","MERGE",FACE,{"derivedFrom":[makeQuery(id+"F26.boolean.opBoolean","MERGE",FACE,{"derivedFrom":[makeQuery(id+"F25.boolean.opBoolean","MERGE",FACE,{"derivedFrom":[makeQuery(id+"F24.boolean.opBoolean","MERGE",FACE,{"derivedFrom":[makeQuery(id+"F13.boolean.opBoolean","MERGE",FACE,{"derivedFrom":[subQ8,subQ2]}),makeQuery(id+"F24.opExtrude","SWEPT_FACE",FACE,{"disambiguationData":[OSD([subQ7]),TDD([makeQuery(id+"F1.opExtrude","CAP_EDGE",EDGE,{"disambiguationData":[OSD([subQ7])],"isStart":false})])]})]}),makeQuery(id+"F25.opExtrude","SWEPT_FACE",FACE,{"disambiguationData":[OSD([subQ4]),TDD([makeQuery(id+"F13.boolean.opBoolean","SPLIT",EDGE,{"disambiguationData":[TD([makeQuery(id+"F3.opExtrude","SWEPT_FACE",FACE,{"disambiguationData":[OSD([subQ6])]})])],"derivedFrom":subQ9})])]}),makeQuery(id+"F25.opExtrude","SWEPT_FACE",FACE,{"disambiguationData":[OSD([subQ4]),TDD([makeQuery(id+"F13.boolean.opBoolean","SPLIT",EDGE,{"disambiguationData":[TD([makeQuery(id+"F3.opExtrude","SWEPT_FACE",FACE,{"disambiguationData":[OSD([subQ3])]})])],"derivedFrom":subQ9})])]})]}),makeQuery(id+"F26.opExtrude","SWEPT_FACE",FACE,{"disambiguationData":[OSD([subQ1]),TDD([makeQuery(id+"F1.opExtrude","CAP_EDGE",EDGE,{"disambiguationData":[OSD([subQ1])],"isStart":false})])]})]}),makeQuery(id+"F27.opExtrude","SWEPT_FACE",FACE,{"disambiguationData":[OSD([subQ0]),TDD([makeQuery(id+"F1.opExtrude","CAP_EDGE",EDGE,{"disambiguationData":[OSD([subQ0])],"isStart":false})])]})]});}
            var sketch = newSketch(context, id + "F29", { "sketchPlane" : qUnion([Q0])});
            skPoint(sketch, "E137", {"position": v(-9.75, 31.75) * mm});
            skLineSegment(sketch, "E138.bottom", {"start": v(-9.75, 31.75) * mm, "end": v(-12.75, 31.75) * mm});
            skLineSegment(sketch, "E138.top", {"start": v(-9.75, 1.75) * mm, "end": v(-12.75, 1.75) * mm});
            skLineSegment(sketch, "E138.left", {"start": v(-9.75, 31.75) * mm, "end": v(-9.75, 1.75) * mm});
            skLineSegment(sketch, "E138.right", {"start": v(-12.75, 31.75) * mm, "end": v(-12.75, 1.75) * mm});
            skLineSegment(sketch, "E139.bottom", {"start": v(-34.25, 31.75) * mm, "end": v(-12.75, 31.75) * mm});
            skLineSegment(sketch, "E139.top", {"start": v(-34.25, -8.25) * mm, "end": v(-12.75, -8.25) * mm});
            skLineSegment(sketch, "E139.right", {"start": v(-12.75, 31.75) * mm, "end": v(-12.75, -8.25) * mm});
            skLineSegment(sketch, "E140.0", {"start": v(-31.25, 28.75) * mm, "end": v(-31.25, -5.25) * mm});
            skLineSegment(sketch, "E140.1", {"start": v(-31.25, 28.75) * mm, "end": v(-15.75, 28.75) * mm});
            skLineSegment(sketch, "E140.2", {"start": v(-15.75, 28.75) * mm, "end": v(-15.75, -5.25) * mm});
            skLineSegment(sketch, "E140.3", {"start": v(-31.25, -5.25) * mm, "end": v(-15.75, -5.25) * mm});
            skLineSegment(sketch, "E141", {"start": v(-34.25, -8.25) * mm, "end": v(-34.25, 31.75) * mm});
            skSolve(sketch);
        }
        {
            var Q0;
            Q0=makeQuery(id+"F29.imprint","IMPRINT",FACE,{"disambiguationData":[TD([[makeQuery(id+"F29.imprint","IMPRINT",EDGE,{"derivedFrom":sQuery(id+"F29.wireOp",EDGE,"E138.bottom")}),1.0]])]});
            extrude(context, id + "F30", {"entities" : qUnion([Q0]), "operationType" : NewBodyOperationType.ADD, "depth" : 21 * mm, "offsetDistance" : 25 * mm});
        }
        {
            var Q0;
            Q0=makeQuery(id+"F13.boolean.opBoolean","COPY",FACE,{"derivedFrom":makeQuery(id+"F13.opExtrude","SWEPT_FACE",FACE,{"disambiguationData":[OSD([sQuery(id+"F12.wireOp",EDGE,"E82.right")])]})});
            extrude(context, id + "F31", {"entities" : qUnion([Q0]), "operationType" : NewBodyOperationType.REMOVE, "oppositeDirection" : true, "depth" : 1 * mm, "offsetDistance" : 25 * mm});
        }
        {
            var Q0;
            Q0=makeQuery(id+"F29.imprint","IMPRINT",FACE,{"disambiguationData":[TD([[makeQuery(id+"F29.imprint","IMPRINT",EDGE,{"derivedFrom":sQuery(id+"F29.wireOp",EDGE,"E140.0")}),1.0]])]});
            extrude(context, id + "F32", {"entities" : qUnion([Q0]), "operationType" : NewBodyOperationType.REMOVE, "oppositeDirection" : true, "depth" : 25 * mm, "offsetDistance" : 25 * mm});
        }
        {
            var Q0;
            Q0=makeQuery(id+"F11.imprint","IMPRINT",FACE,{"disambiguationData":[TD([[makeQuery(id+"F11.imprint","IMPRINT",EDGE,{"derivedFrom":sQuery(id+"F11.wireOp",EDGE,"E78")}),1.0]])]});
            extrude(context, id + "F33", {"entities" : qUnion([Q0]), "operationType" : NewBodyOperationType.REMOVE, "oppositeDirection" : true, "depth" : 25 * mm, "offsetDistance" : 25 * mm});
        }
        {
            var Q0;
            Q0=makeQuery(id+"F11.imprint","IMPRINT",FACE,{"disambiguationData":[TD([[makeQuery(id+"F11.imprint","IMPRINT",EDGE,{"derivedFrom":sQuery(id+"F11.wireOp",EDGE,"E80.0")}),1.0]])]});
            extrude(context, id + "F34", {"entities" : qUnion([Q0]), "operationType" : NewBodyOperationType.REMOVE, "oppositeDirection" : true, "depth" : 25 * mm, "offsetDistance" : 25 * mm});
        }
        {
            var Q0;
            {var subQ0=sQuery(id+"F12.wireOp",EDGE,"E82.right");var subQ1=sQuery(id+"F12.wireOp",EDGE,"E82.bottom");var subQ2=sQuery(id+"F0.wireOp",EDGE,"E0.top");var subQ3=sQuery(id+"F0.wireOp",EDGE,"E0.bottom");var subQ4=sQuery(id+"F0.wireOp",EDGE,"E0.left");var subQ5=makeQuery(id+"F13.opExtrude","SWEPT_FACE",FACE,{"disambiguationData":[OSD([subQ1])]});var subQ6=sQuery(id+"F0.wireOp",EDGE,"E37");var subQ8=sQuery(id+"F0.wireOp",EDGE,"E30");var subQ9=sQuery(id+"F0.wireOp",EDGE,"E0.right");var subQ10=makeQuery(id+"F1.opExtrude","CAP_FACE",FACE,{"disambiguationData":[OSD([subQ3,subQ2,subQ4,subQ9,subQ8,sQuery(id+"F0.wireOp",EDGE,"E31"),sQuery(id+"F0.wireOp",EDGE,"E32"),sQuery(id+"F0.wireOp",EDGE,"E33"),sQuery(id+"F0.wireOp",EDGE,"E34"),sQuery(id+"F0.wireOp",EDGE,"E35"),sQuery(id+"F0.wireOp",EDGE,"E36"),subQ6,sQuery(id+"F0.wireOp",EDGE,"E42"),sQuery(id+"F0.wireOp",EDGE,"E43"),sQuery(id+"F0.wireOp",EDGE,"E44"),sQuery(id+"F0.wireOp",EDGE,"E45")])],"isStart":false});var subQ11=makeQuery(id+"F1.opExtrude","CAP_EDGE",EDGE,{"disambiguationData":[OSD([subQ2])],"isStart":false});Q0=makeQuery(id+"F31.boolean.opBoolean","MERGE",FACE,{"derivedFrom":[makeQuery(id+"F27.boolean.opBoolean","MERGE",FACE,{"derivedFrom":[makeQuery(id+"F26.boolean.opBoolean","MERGE",FACE,{"derivedFrom":[makeQuery(id+"F25.boolean.opBoolean","MERGE",FACE,{"derivedFrom":[makeQuery(id+"F24.boolean.opBoolean","MERGE",FACE,{"derivedFrom":[makeQuery(id+"F13.boolean.opBoolean","MERGE",FACE,{"derivedFrom":[subQ10,subQ5]}),makeQuery(id+"F24.opExtrude","SWEPT_FACE",FACE,{"disambiguationData":[OSD([subQ9]),TDD([makeQuery(id+"F1.opExtrude","CAP_EDGE",EDGE,{"disambiguationData":[OSD([subQ9])],"isStart":false})])]})]}),makeQuery(id+"F25.opExtrude","SWEPT_FACE",FACE,{"disambiguationData":[OSD([subQ2]),TDD([makeQuery(id+"F13.boolean.opBoolean","SPLIT",EDGE,{"disambiguationData":[TD([makeQuery(id+"F3.opExtrude","SWEPT_FACE",FACE,{"disambiguationData":[OSD([subQ8])]})])],"derivedFrom":subQ11})])]}),makeQuery(id+"F25.opExtrude","SWEPT_FACE",FACE,{"disambiguationData":[OSD([subQ2]),TDD([makeQuery(id+"F13.boolean.opBoolean","SPLIT",EDGE,{"disambiguationData":[TD([makeQuery(id+"F3.opExtrude","SWEPT_FACE",FACE,{"disambiguationData":[OSD([subQ6])]})])],"derivedFrom":subQ11})])]})]}),makeQuery(id+"F26.opExtrude","SWEPT_FACE",FACE,{"disambiguationData":[OSD([subQ4]),TDD([makeQuery(id+"F1.opExtrude","CAP_EDGE",EDGE,{"disambiguationData":[OSD([subQ4])],"isStart":false})])]})]}),makeQuery(id+"F27.opExtrude","SWEPT_FACE",FACE,{"disambiguationData":[OSD([subQ3]),TDD([makeQuery(id+"F1.opExtrude","CAP_EDGE",EDGE,{"disambiguationData":[OSD([subQ3])],"isStart":false})])]})]}),makeQuery(id+"F31.opExtrude","SWEPT_FACE",FACE,{"disambiguationData":[OSD([subQ2,subQ1,subQ0])]})]});}
            var sketch = newSketch(context, id + "F35", { "sketchPlane" : qUnion([Q0])});
            skLineSegment(sketch, "E142.bottom", {"start": v(-31.25, -20.75) * mm, "end": v(31.75, -20.75) * mm});
            skLineSegment(sketch, "E142.top", {"start": v(-31.25, -10.75) * mm, "end": v(31.75, -10.75) * mm});
            skLineSegment(sketch, "E142.left", {"start": v(-31.25, -20.75) * mm, "end": v(-31.25, -10.75) * mm});
            skLineSegment(sketch, "E142.right", {"start": v(31.75, -20.75) * mm, "end": v(31.75, -10.75) * mm});
            skSolve(sketch);
        }
        {
            var Q0;
            Q0=makeQuery(id+"F35.imprint","IMPRINT",FACE,{"disambiguationData":[TD([[makeQuery(id+"F35.imprint","IMPRINT",EDGE,{"derivedFrom":sQuery(id+"F35.wireOp",EDGE,"E142.top")}),-1.0]])]});
            extrude(context, id + "F36", {"entities" : qUnion([Q0]), "operationType" : NewBodyOperationType.REMOVE, "oppositeDirection" : true, "depth" : 25 * mm, "offsetDistance" : 25 * mm});
        }
    });
